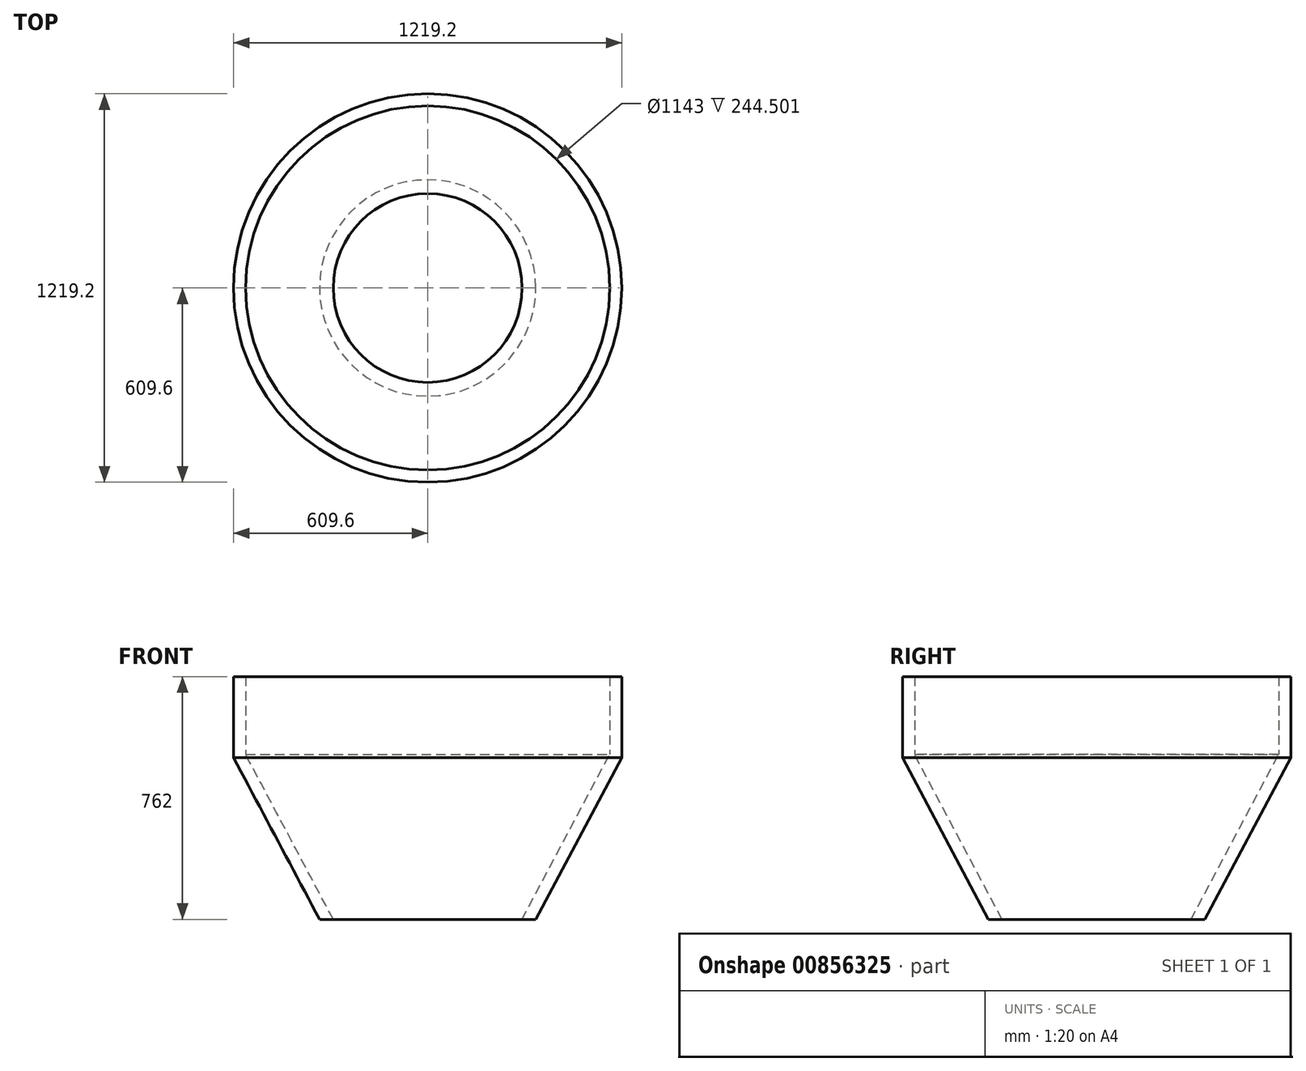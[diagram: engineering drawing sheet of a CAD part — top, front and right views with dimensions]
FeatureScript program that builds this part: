
annotation { "Feature Type Name" : "Feature", "Feature Type Description" : "" }
export const myFeature = defineFeature(function(context is Context, id is Id, definition is map)
    precondition{}
    {
        {
            var Q0;
            Q0=qCreatedBy(makeId("Front.planeOp"),FACE);
            var sketch = newSketch(context, id + "F0", { "sketchPlane" : qUnion([Q0])});
            skLineSegment(sketch, "E0", {"start": v(-609.6, 762) * mm, "end": v(-609.6, 508) * mm});
            skLineSegment(sketch, "E1", {"start": v(-609.6, 508) * mm, "end": v(-609.6, 508) * mm});
            skLineSegment(sketch, "E2", {"start": v(-339.5, 0) * mm, "end": v(-609.6, 508) * mm});
            skLineSegment(sketch, "E3", {"start": v(0, 0) * mm, "end": v(-339.5, 0) * mm});
            skPoint(sketch, "E4.orphan", {"position": v(-234.43, -197.6) * mm});
            skPoint(sketch, "E5", {"position": v(-158.56, 255.57) * mm});
            skLineSegment(sketch, "E6.0", {"start": v(-571.5, 762) * mm, "end": v(-571.5, 517.5) * mm});
            skLineSegment(sketch, "E6.1", {"start": v(-296.34, 0) * mm, "end": v(-571.5, 517.5) * mm});
            skLineSegment(sketch, "E7", {"start": v(-609.6, 762) * mm, "end": v(-571.5, 762) * mm});
            skLineSegment(sketch, "E8", {"start": v(-571.5, 639.75) * mm, "end": v(-571.5, 517.5) * mm});
            skLineSegment(sketch, "E9", {"start": v(0, 0) * mm, "end": v(0, 138.27) * mm});
            skSolve(sketch);
        }
        {
            var Q0;
            Q0=makeQuery(id+"F0.imprint","IMPRINT",FACE,{"disambiguationData":[TD([[makeQuery(id+"F0.imprint","IMPRINT",EDGE,{"derivedFrom":sQuery(id+"F0.wireOp",EDGE,"E0")}),1.0]])]});
            var Q1;
            Q1=sQuery(id+"F0.wireOp",EDGE,"E9");
            revolve(context, id + "F1", {"surfaceOperationType" : NewSurfaceOperationType.NEW, "entities" : qUnion([Q0]), "axis" : qUnion([Q1]), "revolveType" : RevolveType.FULL});
        }
    });
